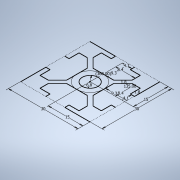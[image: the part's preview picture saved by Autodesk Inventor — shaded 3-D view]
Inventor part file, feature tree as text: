
AUTODESK INVENTOR PART (.ipt)
format: ipt  version: 2022 (Build 260153000, 153)  size: 120,320 bytes
history: native  units: mm
features: sketch x1
ambient origin geometry x8: Origin, YZ Plane, XZ Plane, XY Plane, X Axis, Y Axis, Z Axis, Center Point
feature tree (1):
  sketch  "Sketch1"  dims[d0=30.0mm d1=30.0mm d2=15.0mm d3=15.0mm d4=8.4mm d5=8.4mm d6=4.1mm d7=4.1mm d8=1.8mm d9=9.3mm d10=9.3mm d11=1.8mm d12=135.0deg d13=40.0mm d15=360.0deg d17=6.8mm]
